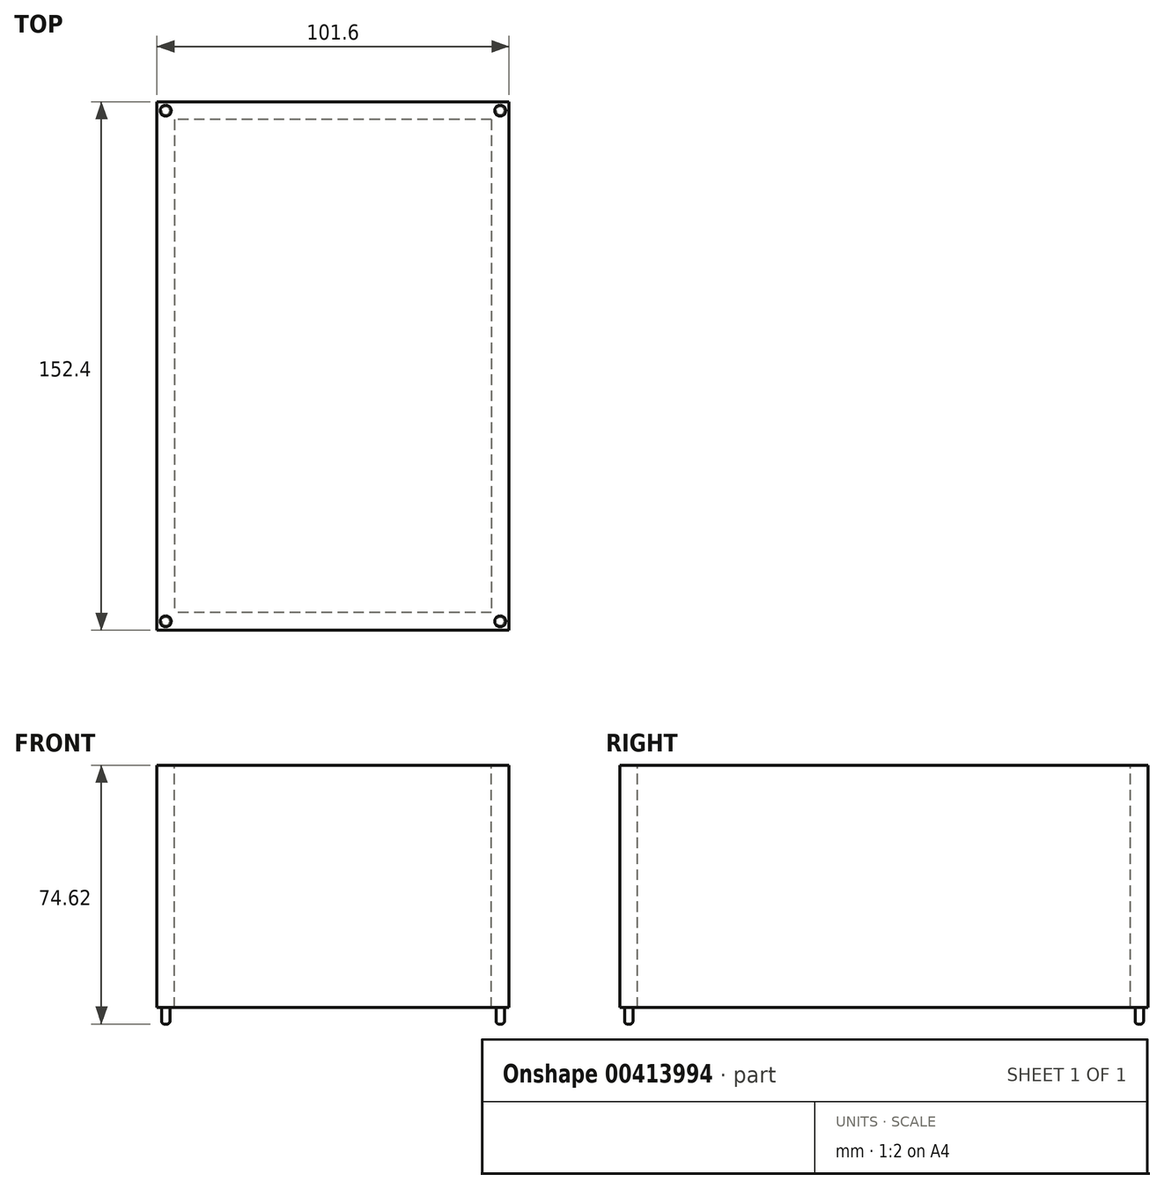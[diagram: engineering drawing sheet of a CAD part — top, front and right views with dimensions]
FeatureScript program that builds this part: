
annotation { "Feature Type Name" : "Feature", "Feature Type Description" : "" }
export const myFeature = defineFeature(function(context is Context, id is Id, definition is map)
    precondition{}
    {
        {
            var Q0;
            Q0=qCreatedBy(makeId("Top.planeOp"),FACE);
            var sketch = newSketch(context, id + "F0", { "sketchPlane" : qUnion([Q0])});
            skLineSegment(sketch, "E0.bottom", {"start": v(50.8, 76.2) * mm, "end": v(-50.8, 76.2) * mm});
            skLineSegment(sketch, "E0.top", {"start": v(50.8, -76.2) * mm, "end": v(-50.8, -76.2) * mm});
            skLineSegment(sketch, "E0.left", {"start": v(50.8, 76.2) * mm, "end": v(50.8, -76.2) * mm});
            skLineSegment(sketch, "E0.right", {"start": v(-50.8, 76.2) * mm, "end": v(-50.8, -76.2) * mm});
            skPoint(sketch, "E0.middle", {"position": v(0, 0) * mm});
            skLineSegment(sketch, "E1.0", {"start": v(-45.72, 71.12) * mm, "end": v(-45.72, -71.12) * mm});
            skLineSegment(sketch, "E1.1", {"start": v(45.72, 71.12) * mm, "end": v(-45.72, 71.12) * mm});
            skLineSegment(sketch, "E1.2", {"start": v(45.72, 71.12) * mm, "end": v(45.72, -71.12) * mm});
            skLineSegment(sketch, "E1.3", {"start": v(45.72, -71.12) * mm, "end": v(-45.72, -71.12) * mm});
            skLineSegment(sketch, "E2", {"start": v(-45.72, -71.12) * mm, "end": v(-50.8, -76.2) * mm, "construction": true});
            skPoint(sketch, "E3", {"position": v(-48.26, -73.66) * mm});
            skCircle(sketch, "E4", {"center": v(-48.26, -73.66) * mm, "radius": 1.59 * mm});
            skLineSegment(sketch, "E5", {"start": v(45.72, -71.12) * mm, "end": v(50.8, -76.2) * mm, "construction": true});
            skCircle(sketch, "E6", {"center": v(48.26, -73.66) * mm, "radius": 1.59 * mm});
            skLineSegment(sketch, "E7", {"start": v(45.72, 71.12) * mm, "end": v(50.8, 76.2) * mm, "construction": true});
            skCircle(sketch, "E8", {"center": v(48.26, 73.66) * mm, "radius": 1.59 * mm});
            skLineSegment(sketch, "E9", {"start": v(-45.72, 71.12) * mm, "end": v(-50.8, 76.2) * mm, "construction": true});
            skCircle(sketch, "E10", {"center": v(-48.26, 73.66) * mm, "radius": 1.59 * mm});
            skSolve(sketch);
        }
        {
            var Q0;
            Q0=makeQuery(id+"F0.imprint","IMPRINT",FACE,{"disambiguationData":[TD([[makeQuery(id+"F0.imprint","IMPRINT",EDGE,{"derivedFrom":sQuery(id+"F0.wireOp",EDGE,"E0.bottom")}),1.0]])]});
            var Q1;
            Q1=makeQuery(id+"F0.imprint","IMPRINT",FACE,{"disambiguationData":[TD([[makeQuery(id+"F0.imprint","IMPRINT",EDGE,{"derivedFrom":sQuery(id+"F0.wireOp",EDGE,"E1.0")}),1.0]])]});
            extrude(context, id + "F1", {"entities" : qUnion([Q0, Q1]), "depth" : 1 / 101.6 * mm});
        }
        {
            var Q0;
            Q0=makeQuery(id+"F0.imprint","IMPRINT",FACE,{"disambiguationData":[TD([[makeQuery(id+"F0.imprint","IMPRINT",EDGE,{"derivedFrom":sQuery(id+"F0.wireOp",EDGE,"E0.bottom")}),1.0]])]});
            var Q1;
            Q1=makeQuery(id+"F0.imprint","IMPRINT",FACE,{"disambiguationData":[TD([[makeQuery(id+"F0.imprint","IMPRINT",EDGE,{"derivedFrom":sQuery(id+"F0.wireOp",EDGE,"E6")}),1.0]])]});
            var Q2;
            Q2=makeQuery(id+"F0.imprint","IMPRINT",FACE,{"disambiguationData":[TD([[makeQuery(id+"F0.imprint","IMPRINT",EDGE,{"derivedFrom":sQuery(id+"F0.wireOp",EDGE,"E4")}),1.0]])]});
            var Q3;
            Q3=makeQuery(id+"F0.imprint","IMPRINT",FACE,{"disambiguationData":[TD([[makeQuery(id+"F0.imprint","IMPRINT",EDGE,{"derivedFrom":sQuery(id+"F0.wireOp",EDGE,"E10")}),1.0]])]});
            var Q4;
            Q4=makeQuery(id+"F0.imprint","IMPRINT",FACE,{"disambiguationData":[TD([[makeQuery(id+"F0.imprint","IMPRINT",EDGE,{"derivedFrom":sQuery(id+"F0.wireOp",EDGE,"E8")}),1.0]])]});
            extrude(context, id + "F2", {"entities" : qUnion([Q0, Q1, Q2, Q3, Q4]), "operationType" : NewBodyOperationType.ADD, "oppositeDirection" : true, "depth" : 69.85 * mm});
        }
        {
            var Q0;
            Q0=makeQuery(id+"F2.opExtrude","CAP_FACE",FACE,{"disambiguationData":[OSD([sQuery(id+"F0.wireOp",EDGE,"E0.bottom"),sQuery(id+"F0.wireOp",EDGE,"E0.top"),sQuery(id+"F0.wireOp",EDGE,"E0.left"),sQuery(id+"F0.wireOp",EDGE,"E0.right"),sQuery(id+"F0.wireOp",EDGE,"E1.0"),sQuery(id+"F0.wireOp",EDGE,"E1.1"),sQuery(id+"F0.wireOp",EDGE,"E1.2"),sQuery(id+"F0.wireOp",EDGE,"E1.3")])],"isStart":false});
            var sketch = newSketch(context, id + "F3", { "sketchPlane" : qUnion([Q0])});
            skLineSegment(sketch, "E11", {"start": v(45.72, 71.12) * mm, "end": v(50.8, 76.2) * mm, "construction": true});
            skLineSegment(sketch, "E12", {"start": v(45.72, -71.12) * mm, "end": v(50.8, -76.2) * mm, "construction": true});
            skLineSegment(sketch, "E13", {"start": v(-45.72, -71.12) * mm, "end": v(-50.8, -76.2) * mm, "construction": true});
            skLineSegment(sketch, "E14", {"start": v(-50.8, 76.2) * mm, "end": v(-45.72, 71.12) * mm, "construction": true});
            skCircle(sketch, "E15", {"center": v(48.26, 73.66) * mm, "radius": 1.2 * mm});
            skCircle(sketch, "E16", {"center": v(48.26, -73.66) * mm, "radius": 1.2 * mm});
            skCircle(sketch, "E17", {"center": v(-48.26, -73.66) * mm, "radius": 1.2 * mm});
            skCircle(sketch, "E18", {"center": v(-48.26, 73.66) * mm, "radius": 1.2 * mm});
            skSolve(sketch);
        }
        {
            var Q0;
            Q0=makeQuery(id+"F3.imprint","IMPRINT",FACE,{"disambiguationData":[TD([[makeQuery(id+"F3.imprint","IMPRINT",EDGE,{"derivedFrom":sQuery(id+"F3.wireOp",EDGE,"E15")}),1.0]])]});
            var Q1;
            Q1=makeQuery(id+"F3.imprint","IMPRINT",FACE,{"disambiguationData":[TD([[makeQuery(id+"F3.imprint","IMPRINT",EDGE,{"derivedFrom":sQuery(id+"F3.wireOp",EDGE,"E16")}),1.0]])]});
            var Q2;
            Q2=makeQuery(id+"F3.imprint","IMPRINT",FACE,{"disambiguationData":[TD([[makeQuery(id+"F3.imprint","IMPRINT",EDGE,{"derivedFrom":sQuery(id+"F3.wireOp",EDGE,"E17")}),1.0]])]});
            var Q3;
            Q3=makeQuery(id+"F3.imprint","IMPRINT",FACE,{"disambiguationData":[TD([[makeQuery(id+"F3.imprint","IMPRINT",EDGE,{"derivedFrom":sQuery(id+"F3.wireOp",EDGE,"E18")}),1.0]])]});
            extrude(context, id + "F4", {"entities" : qUnion([Q0, Q1, Q2, Q3]), "operationType" : NewBodyOperationType.ADD, "depth" : 4.76 * mm});
        }
        {
            var Q0;
            Q0=makeQuery(id+"F4.opExtrude","CAP_EDGE",EDGE,{"disambiguationData":[OSD([sQuery(id+"F3.wireOp",EDGE,"E15")])],"isStart":false});
            var Q1;
            Q1=makeQuery(id+"F4.opExtrude","CAP_EDGE",EDGE,{"disambiguationData":[OSD([sQuery(id+"F3.wireOp",EDGE,"E18")])],"isStart":false});
            var Q2;
            Q2=makeQuery(id+"F4.opExtrude","CAP_EDGE",EDGE,{"disambiguationData":[OSD([sQuery(id+"F3.wireOp",EDGE,"E17")])],"isStart":false});
            var Q3;
            Q3=makeQuery(id+"F4.opExtrude","CAP_EDGE",EDGE,{"disambiguationData":[OSD([sQuery(id+"F3.wireOp",EDGE,"E16")])],"isStart":false});
            fillet(context, id + "F5", {"entities" : qUnion([Q0, Q1, Q2, Q3]), "radius" : 0.76 * mm, "tangentPropagation" : true, "allowEdgeOverflow" : false});
        }
        {
            var Q0;
            Q0=makeQuery(id+"F1.opExtrude","CAP_EDGE",EDGE,{"disambiguationData":[OSD([sQuery(id+"F0.wireOp",EDGE,"E4")])],"isStart":false});
            var Q1;
            Q1=makeQuery(id+"F1.opExtrude","CAP_EDGE",EDGE,{"disambiguationData":[OSD([sQuery(id+"F0.wireOp",EDGE,"E10")])],"isStart":false});
            var Q2;
            Q2=makeQuery(id+"F1.opExtrude","CAP_EDGE",EDGE,{"disambiguationData":[OSD([sQuery(id+"F0.wireOp",EDGE,"E8")])],"isStart":false});
            var Q3;
            Q3=makeQuery(id+"F1.opExtrude","CAP_EDGE",EDGE,{"disambiguationData":[OSD([sQuery(id+"F0.wireOp",EDGE,"E6")])],"isStart":false});
            fillet(context, id + "F6", {"entities" : qUnion([Q0, Q1, Q2, Q3]), "radius" : 0.5 * mm, "tangentPropagation" : true, "allowEdgeOverflow" : false});
        }
    });
